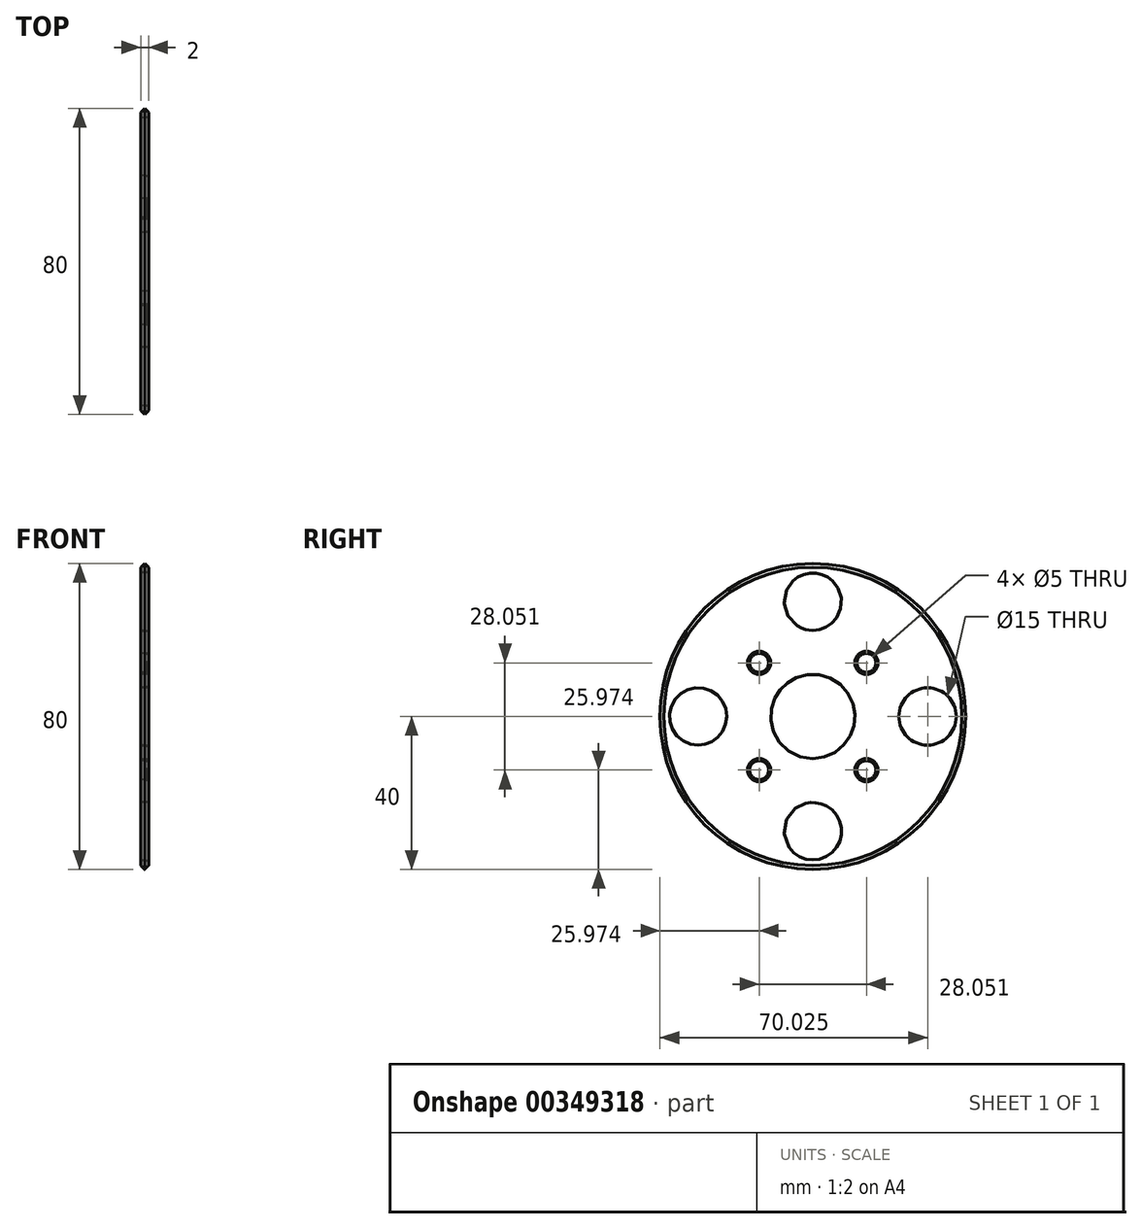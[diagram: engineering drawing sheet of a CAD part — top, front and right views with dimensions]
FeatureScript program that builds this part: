
annotation { "Feature Type Name" : "Feature", "Feature Type Description" : "" }
export const myFeature = defineFeature(function(context is Context, id is Id, definition is map)
    precondition{}
    {
        {
            var Q0;
            Q0=qCreatedBy(makeId("Right.planeOp"),FACE);
            var sketch = newSketch(context, id + "F0", { "sketchPlane" : qUnion([Q0])});
            skCircle(sketch, "E0", {"center": v(0, 0) * mm, "radius": 40 * mm});
            skCircle(sketch, "E1", {"center": v(0, 0) * mm, "radius": 11.02 * mm});
            skPoint(sketch, "E2.0.midPoint", {"position": v(0, 14.03) * mm});
            skCircle(sketch, "E3", {"center": v(-14.03, 14.03) * mm, "radius": 2.5 * mm});
            skCircle(sketch, "E4", {"center": v(14.03, 14.03) * mm, "radius": 2.5 * mm});
            skCircle(sketch, "E5", {"center": v(14.03, -14.03) * mm, "radius": 2.5 * mm});
            skCircle(sketch, "E6", {"center": v(-14.03, -14.03) * mm, "radius": 2.5 * mm});
            skCircle(sketch, "E7", {"center": v(0, 0) * mm, "radius": 30.02 * mm});
            skCircle(sketch, "E8", {"center": v(0, 30.02) * mm, "radius": 7.5 * mm});
            skCircle(sketch, "E9", {"center": v(-30.02, 0) * mm, "radius": 7.5 * mm});
            skCircle(sketch, "E10", {"center": v(30.02, 0) * mm, "radius": 7.5 * mm});
            skCircle(sketch, "E11", {"center": v(0, -30.02) * mm, "radius": 7.5 * mm});
            skSolve(sketch);
        }
        {
            var Q0;
            Q0=makeQuery(id+"F0.imprint","IMPRINT",FACE,{"disambiguationData":[TD([[makeQuery(id+"F0.imprint","IMPRINT",EDGE,{"derivedFrom":sQuery(id+"F0.wireOp",EDGE,"E0")}),1.0]])]});
            var Q1;
            Q1=makeQuery(id+"F0.imprint","IMPRINT",FACE,{"disambiguationData":[TD([[makeQuery(id+"F0.imprint","IMPRINT",EDGE,{"derivedFrom":sQuery(id+"F0.wireOp",EDGE,"E1")}),-1.0]])]});
            extrude(context, id + "F1", {"entities" : qUnion([Q0, Q1]), "depth" : 2 * mm});
        }
        {
            var Q0;
            Q0=makeQuery(id+"F1.opExtrude","CAP_EDGE",EDGE,{"disambiguationData":[OSD([sQuery(id+"F0.wireOp",EDGE,"E1")])],"isStart":true});
            var Q1;
            Q1=makeQuery(id+"F1.opExtrude","SWEPT_FACE",FACE,{"disambiguationData":[OSD([sQuery(id+"F0.wireOp",EDGE,"E1")])]});
            fillet(context, id + "F2", {"entities" : qUnion([Q0, Q1]), "radius" : 1 * mm, "tangentPropagation" : true, "allowEdgeOverflow" : false});
        }
        {
            var Q0;
            Q0=makeQuery(id+"F1.opExtrude","CAP_EDGE",EDGE,{"disambiguationData":[OSD([sQuery(id+"F0.wireOp",EDGE,"E0")])],"isStart":true});
            var Q1;
            Q1=makeQuery(id+"F1.opExtrude","CAP_EDGE",EDGE,{"disambiguationData":[OSD([sQuery(id+"F0.wireOp",EDGE,"E0")])],"isStart":false});
            chamfer(context, id + "F3", {"entities" : qUnion([Q0, Q1]), "width" : 1 * mm, "tangentPropagation" : true});
        }
        {
            var Q0;
            Q0=makeQuery(id+"F1.opExtrude","CAP_EDGE",EDGE,{"disambiguationData":[OSD([sQuery(id+"F0.wireOp",EDGE,"E4")])],"isStart":false});
            var Q1;
            Q1=makeQuery(id+"F1.opExtrude","CAP_EDGE",EDGE,{"disambiguationData":[OSD([sQuery(id+"F0.wireOp",EDGE,"E5")])],"isStart":false});
            var Q2;
            Q2=makeQuery(id+"F1.opExtrude","CAP_EDGE",EDGE,{"disambiguationData":[OSD([sQuery(id+"F0.wireOp",EDGE,"E6")])],"isStart":false});
            var Q3;
            Q3=makeQuery(id+"F1.opExtrude","CAP_EDGE",EDGE,{"disambiguationData":[OSD([sQuery(id+"F0.wireOp",EDGE,"E3")])],"isStart":false});
            chamfer(context, id + "F4", {"entities" : qUnion([Q0, Q1, Q2, Q3]), "width" : 0.5 * mm, "tangentPropagation" : true});
        }
        {
            var Q0;
            Q0=makeQuery(id+"F1.opExtrude","CAP_EDGE",EDGE,{"disambiguationData":[OSD([sQuery(id+"F0.wireOp",EDGE,"E8")])],"isStart":false});
            var Q1;
            Q1=makeQuery(id+"F1.opExtrude","CAP_EDGE",EDGE,{"disambiguationData":[OSD([sQuery(id+"F0.wireOp",EDGE,"E10")])],"isStart":false});
            var Q2;
            Q2=makeQuery(id+"F1.opExtrude","CAP_EDGE",EDGE,{"disambiguationData":[OSD([sQuery(id+"F0.wireOp",EDGE,"E11")])],"isStart":false});
            var Q3;
            Q3=makeQuery(id+"F1.opExtrude","CAP_EDGE",EDGE,{"disambiguationData":[OSD([sQuery(id+"F0.wireOp",EDGE,"E9")])],"isStart":false});
            var Q4;
            Q4=makeQuery(id+"F1.opExtrude","CAP_EDGE",EDGE,{"disambiguationData":[OSD([sQuery(id+"F0.wireOp",EDGE,"E9")])],"isStart":true});
            var Q5;
            Q5=makeQuery(id+"F1.opExtrude","CAP_EDGE",EDGE,{"disambiguationData":[OSD([sQuery(id+"F0.wireOp",EDGE,"E8")])],"isStart":true});
            var Q6;
            Q6=makeQuery(id+"F1.opExtrude","CAP_EDGE",EDGE,{"disambiguationData":[OSD([sQuery(id+"F0.wireOp",EDGE,"E11")])],"isStart":true});
            fillet(context, id + "F5", {"entities" : qUnion([Q0, Q1, Q2, Q3, Q4, Q5, Q6]), "radius" : 1 * mm, "tangentPropagation" : true, "allowEdgeOverflow" : false});
        }
    });
